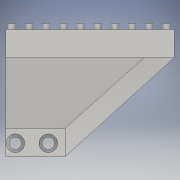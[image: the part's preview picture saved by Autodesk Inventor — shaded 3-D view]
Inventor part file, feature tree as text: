
AUTODESK INVENTOR PART (.ipt)
format: ipt  version: 2016 (Build 200138000, 138)  size: 689,152 bytes
history: native  units: in
note: dims shown in document units (in); Inventor stores cm internally (conversion verified against a paired STEP export)
features: sketch x11, loft x4, other x4, extrude x3, sweep x1, hole x1
ambient origin geometry x8: Origin, YZ Plane, XZ Plane, XY Plane, X Axis, Y Axis, Z Axis, Center Point
bodies: Solid1 (feature_tree)
feature tree (24):
  extrude  "Extrusion1"  Depth=0.5in
  extrude  "Extrusion2"  Depth=0.5in TaperAngle=0.0deg
  sketch  "Sketch4"  dims[d22=0.75in d23=0.0in d25=0.0125in]
  sketch  "Sketch6"  dims[d41=1.0in d55=0.0in d56=0.0in]
  sweep  "Sweep4"
  sketch  "Sketch10"  dims[d57=0.0in d58=90.0deg d59=0.0in d60=90.0deg]
  sketch  "Sketch11"  dims[d61=0.0in d62=90.0deg d63=0.0in d64=90.0deg]
  loft  "Loft2"
  loft  "Loft3"
  sketch  "Sketch12"  dims[d65=0.0in d66=90.0deg d67=0.0in d68=90.0deg]
  sketch  "Sketch13"  dims[d69=0.0in d70=90.0deg d71=0.0in d72=90.0deg]
  sketch  "Sketch14"  dims[d81=3.937in d83=0.2165in d84=1.9685in d86=0.2087in d89=0.0787in d90=0.0in]
  loft  "Loft4"
  loft  "Loft5"
  extrude  "Extrusion5"  TaperAngle=0.0deg  [1 undecoded]
  hole  "Hole6"  [1 undecoded]
  sketch  "Sketch1"  dims[d0=0.75in d1=0.5in]
  sketch  "Sketch3"  dims[d2=0.4173in d3=0.5in d4=0.0in]
  other  "Edges3"
  other  "Edges4"
  other  "Edges5"
  other  "Edges6"
  sketch  "Sketch16"  dims[d91=0.4173in]
  sketch  "Sketch17"  dims[d92=0.1575in d93=0.75in d94=0.2362in d95=0.1181in d96=0.5635in d97=1.0in d98=0.8108in d5=1.0in d6=1.0in]
note: 2 required parameter values undecoded (feature->parameter linkage not recoverable at this tier; creation-order binding heuristic only, values carry confidence <= 0.55)
